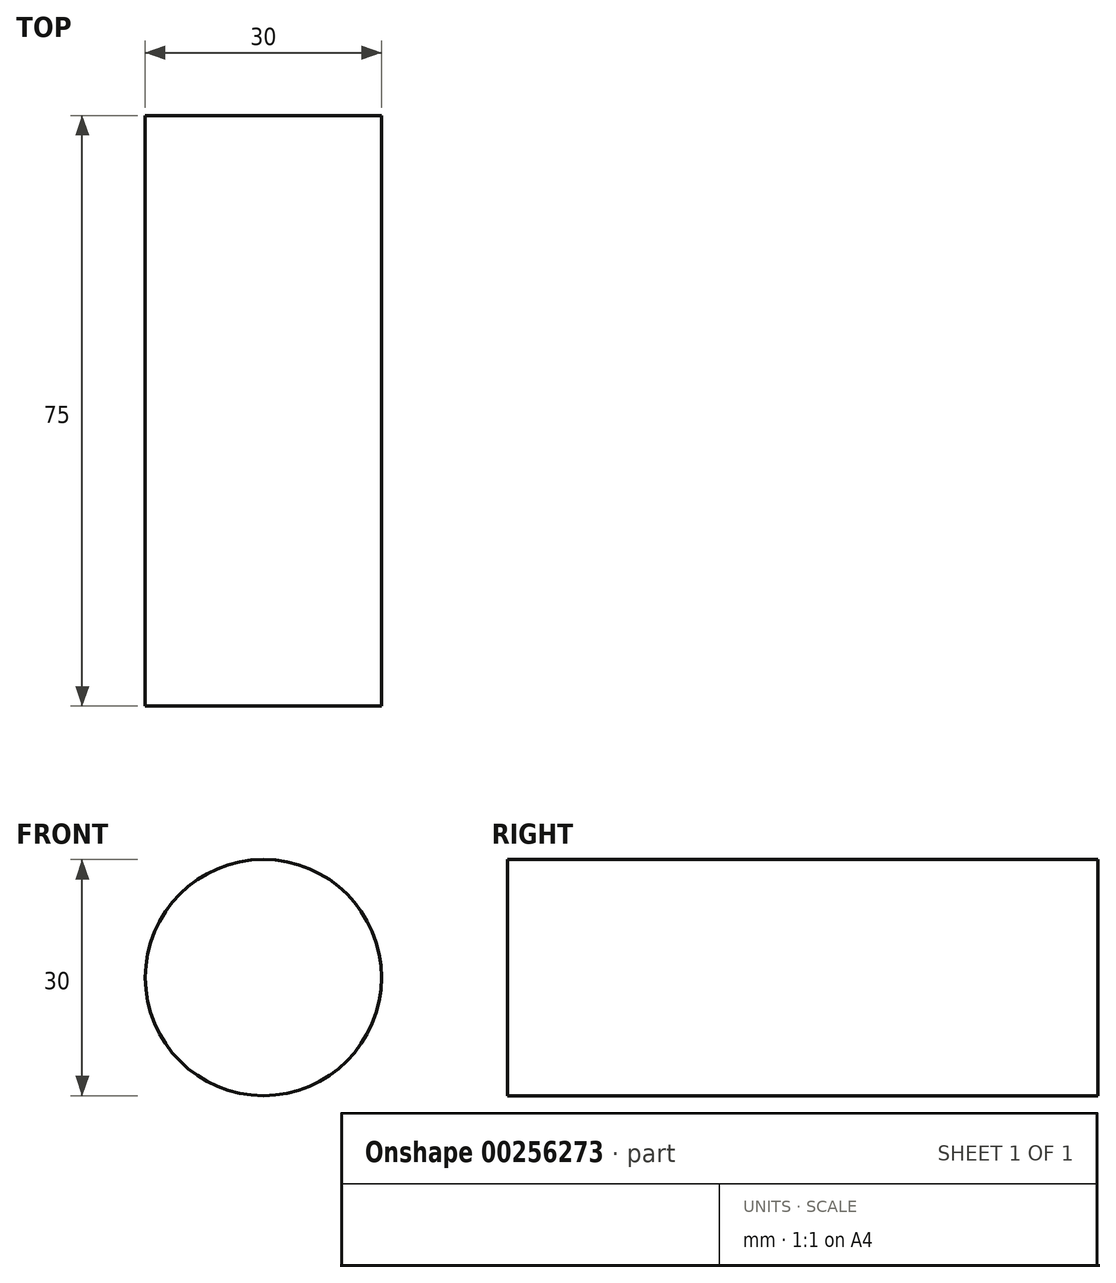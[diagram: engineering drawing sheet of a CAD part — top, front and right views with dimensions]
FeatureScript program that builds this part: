
annotation { "Feature Type Name" : "Feature", "Feature Type Description" : "" }
export const myFeature = defineFeature(function(context is Context, id is Id, definition is map)
    precondition{}
    {
        {
            var Q0;
            Q0=qCreatedBy(makeId("Front.planeOp"),FACE);
            var sketch = newSketch(context, id + "F0", { "sketchPlane" : qUnion([Q0])});
            skCircle(sketch, "E0", {"center": v(0, 0) * mm, "radius": 15 * mm});
            skSolve(sketch);
        }
        {
            var Q0;
            Q0 = qSketchRegion(id + "F0", true);
            extrude(context, id + "F1", {"entities" : qUnion([Q0]), "depth" : 25 * mm});
        }
        {
            var Q0;
            Q0=makeQuery(id+"F1.opExtrude","CAP_FACE",FACE,{"disambiguationData":[OSD([sQuery(id+"F0.wireOp",EDGE,"E0")])],"isStart":false});
            extrude(context, id + "F2", {"entities" : qUnion([Q0]), "operationType" : NewBodyOperationType.ADD, "depth" : 25 * mm});
        }
        {
            var Q0;
            Q0=makeQuery(id+"F2.opExtrude","CAP_FACE",FACE,{"disambiguationData":[OSD([sQuery(id+"F0.wireOp",EDGE,"E0")])],"isStart":false});
            extrude(context, id + "F3", {"entities" : qUnion([Q0]), "operationType" : NewBodyOperationType.ADD, "depth" : 25 * mm});
        }
    });
